# Revit family: bottle_filling_station_ mechanically _activated -elkay-LMABFDWSSK
name_source: partatom
category: Plumbing Fixtures
units: mm (PartAtom-declared; Revit-internal decimal feet)

## family parameters
Always vertical = Yes
Cut with Voids When Loaded = No
Maintain Annotation Orientation = No
OmniClass Number = 23.65.70.14.11
OmniClass Title = Drinking Fountains/Coolers
Part Type = Normal
Room Calculation Point = No
Round Connector Dimension = Use Diameter
Shared = No
Work Plane-Based = No

## types (1)
- LMABFDWSSK (Bottle Filling Station with Mechanically Activated Single ADA Cooler)
    Activation Method = Electronic Bottle Filler Sensor with Mechanical Front and Side Bubbler Pushbar
    Approx. Shipping Weight (lbs) = 57
    Assembly Code = D2010.60
    CWFU = 0
    Chilling Capacity (GPH) = 0
    Connector Outlet B = 1.25 "
    Connector Supply A = 0.375 "
    Current = 0 A
    Default Elevation = 0 "
    Description = ezH2O® Bottle Filling Station with Mechanically Activated Single ADA Cooler Filtered Non Refrigerated Stainless
    Floor to waste outlet = 25 "
    Floor to water supply loaction = 18.38 "
    HWFU = 0
    Inlet Connection Size (inch) = 0.375 "
    Installation Location = Indoor
    Main Material = Finish-Elkay- Steel
    Manufacturer = Elkay Manufacturer Company
    Manufacturer Brand = Elkay (by Zurn Elkay Water Solutions)
    Model = LMABFDWSSK
    Mounting Type = Wall Mount (On Wall)
    Number of Poles = 1
    Outlet Connection Size (inch) = 1.25 "
    Power Factor = 1
    Product Documentation Link = https://www.elkayfiles.com
    Product Installation Sheet URL = https://www.elkayfiles.com
    Product Page URL = https://www.elkay.com
    Product Weight (lbs) = 45
    Product data URL = https://www.bimobject.com
    Repair Parts URL = https://www.elkayfiles.com
    URL = https://www.elkay.com
    Voltage = 115 V
    WFU = 0

## geometry (parser evidence)
native form markers: Sweep x10
no freeform markers — native parametric forms only
